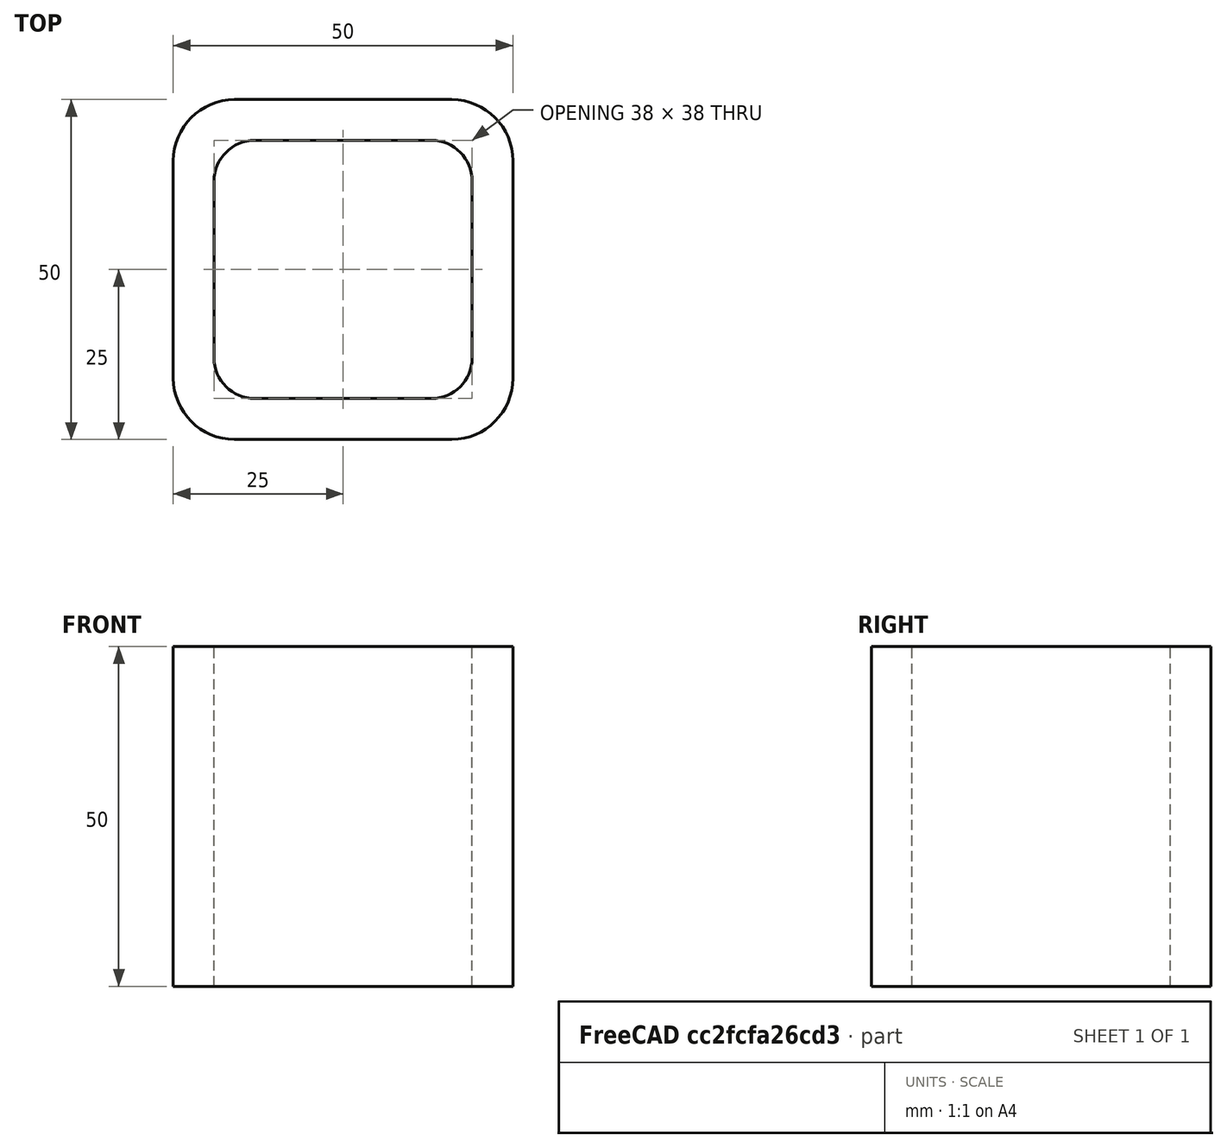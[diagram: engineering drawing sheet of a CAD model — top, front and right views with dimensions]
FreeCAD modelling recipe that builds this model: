
FCSTD DOCUMENT  (FreeCAD 0.15R4671 (Git))
Label: Square hollow section 50x50x6 EN10219 S235JRH
License: All rights reserved
LicenseURL: http://en.wikipedia.org/wiki/All_rights_reserved
objects: Sketcher::SketchObject×1, Part::Extrusion×1
note: 2 computed .brp shape members not serialized (recipe doc carries the construction recipe); baked Part::Feature solids carry a one-line shape summary decoded from their .brp

FEATURE [Sketcher::SketchObject] Sketch
  sketch-geometry (16):
    g0: LineSegment StartX=-13 StartY=19 StartZ=0 EndX=13 EndY=19 EndZ=0
    g1: LineSegment StartX=19 StartY=13 StartZ=0 EndX=19 EndY=-13 EndZ=0
    g2: LineSegment StartX=13 StartY=-19 StartZ=0 EndX=-13 EndY=-19 EndZ=0
    g3: LineSegment StartX=-19 StartY=-13 StartZ=0 EndX=-19 EndY=13 EndZ=0
    g4: LineSegment StartX=-16 StartY=25 StartZ=0 EndX=16 EndY=25 EndZ=0
    g5: LineSegment StartX=25 StartY=16 StartZ=0 EndX=25 EndY=-16 EndZ=0
    g6: LineSegment StartX=16 StartY=-25 StartZ=0 EndX=-16 EndY=-25 EndZ=0
    g7: LineSegment StartX=-25 StartY=-16 StartZ=0 EndX=-25 EndY=16 EndZ=0
    g8: ArcOfCircle CenterX=-13 CenterY=13 CenterZ=0 NormalX=0 NormalY=0 NormalZ=1 Radius=6 StartAngle=1.5708 EndAngle=3.14159
    g9: ArcOfCircle CenterX=13 CenterY=13 CenterZ=0 NormalX=0 NormalY=0 NormalZ=1 Radius=6 StartAngle=0 EndAngle=1.5708
    g10: ArcOfCircle CenterX=13 CenterY=-13 CenterZ=0 NormalX=0 NormalY=0 NormalZ=1 Radius=6 StartAngle=4.71239 EndAngle=6.28319
    g11: ArcOfCircle CenterX=-13 CenterY=-13 CenterZ=0 NormalX=0 NormalY=0 NormalZ=1 Radius=6 StartAngle=3.14159 EndAngle=4.71239
    g12: ArcOfCircle CenterX=16 CenterY=16 CenterZ=0 NormalX=0 NormalY=0 NormalZ=1 Radius=9 StartAngle=0 EndAngle=1.5708
    g13: ArcOfCircle CenterX=16 CenterY=-16 CenterZ=0 NormalX=0 NormalY=0 NormalZ=1 Radius=9 StartAngle=4.71239 EndAngle=6.28319
    g14: ArcOfCircle CenterX=-16 CenterY=-16 CenterZ=0 NormalX=0 NormalY=0 NormalZ=1 Radius=9 StartAngle=3.14159 EndAngle=4.71239
    g15: ArcOfCircle CenterX=-16 CenterY=16 CenterZ=0 NormalX=0 NormalY=0 NormalZ=1 Radius=9 StartAngle=1.5708 EndAngle=3.14159
  constraints (36):
    c: Horizontal(g2)
    c: Vertical(g3)
    c: Horizontal(g6)
    c: Vertical(g7)
    c: Tangent(g3,g8) = 1.5708
    c: Tangent(g0,g8) = 1.5708
    c: Tangent(g0,g9) = 1.5708
    c: Tangent(g1,g9) = 1.5708
    c: Tangent(g1,g10) = 1.5708
    c: Tangent(g2,g10) = 1.5708
    c: Tangent(g2,g11) = 1.5708
    c: Tangent(g3,g11) = 1.5708
    c: Tangent(g4,g12) = 1.5708
    c: Tangent(g5,g12) = 1.5708
    c: Tangent(g5,g13) = 1.5708
    c: Tangent(g6,g13) = 1.5708
    c: Tangent(g6,g14) = 1.5708
    c: Tangent(g7,g14) = 1.5708
    c: Tangent(g7,g15) = 1.5708
    c: Tangent(g4,g15) = 1.5708
    c: Equal(g9,g8)
    c: Equal(g9,g11)
    c: Equal(g9,g10)
    c: Equal(g12,g15)
    c: Equal(g12,g14)
    c: Equal(g12,g13)
    c: Symmetric(g4,g6,g-1)
    c: Symmetric(g7,g5,g-2)
    c: DistanceY(g4,g6) = -50
    c: DistanceX(g7,g5) = 50
    c: Symmetric(g3,g1,g-2)
    c: Symmetric(g0,g2,g-1)
    c: DistanceY(g0,g4) = 6
    c: DistanceX(g5,g1) = -6
    c: Radius(g9) = 6
    c: Radius(g12) = 9
FEATURE [Part::Extrusion] Extrude  label="Square hollow section 50x50x6 EN10219 S235JRH"
  Base = -> Sketch
  Dir = (0,0,50)
  Solid = true
